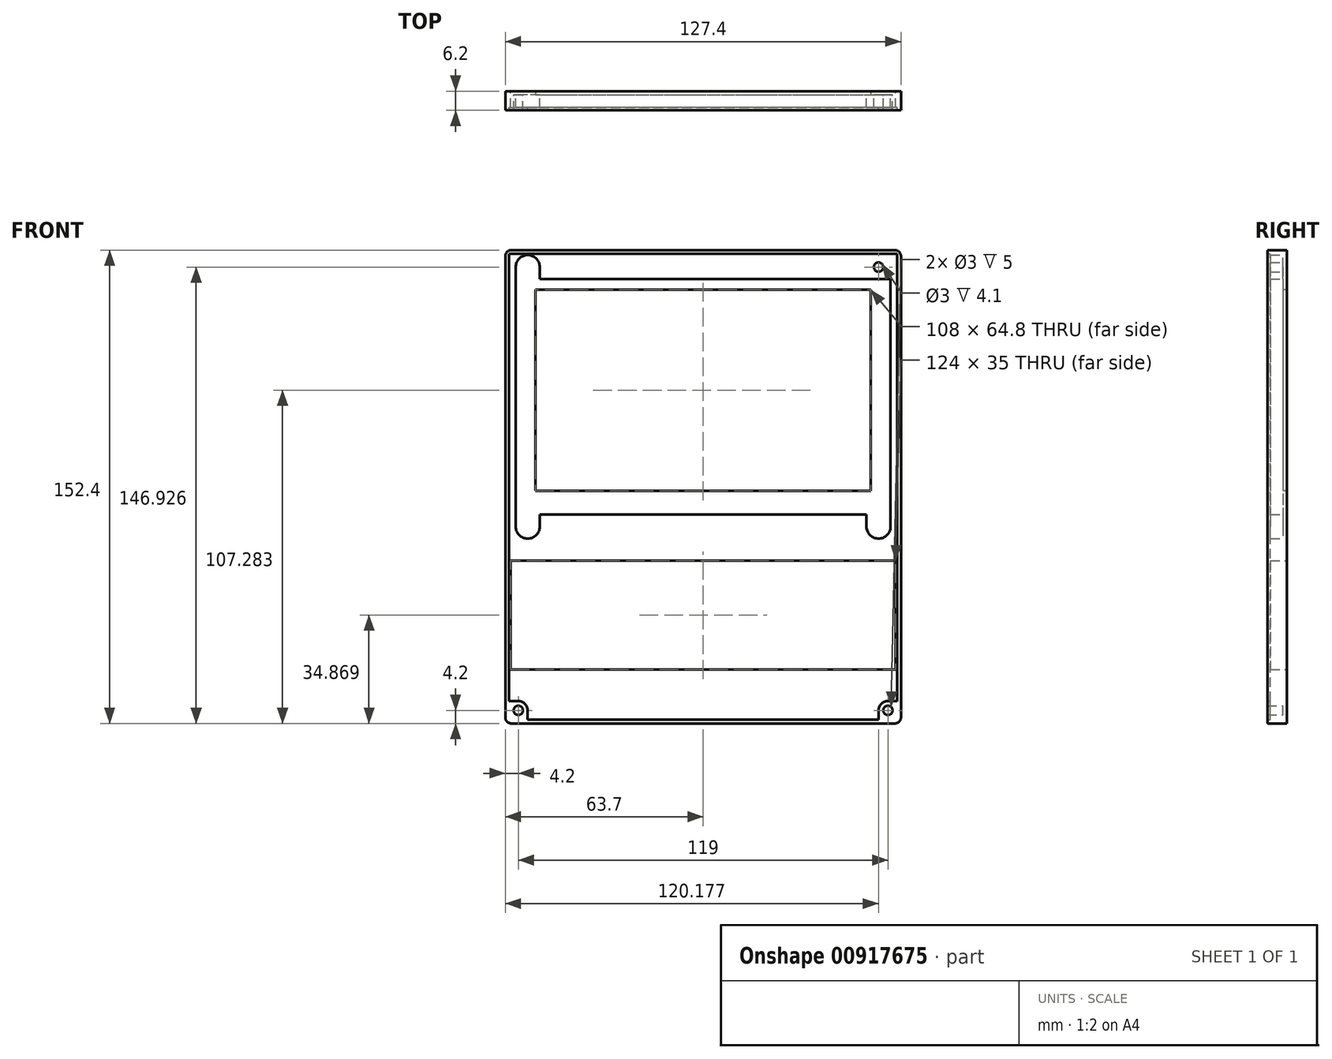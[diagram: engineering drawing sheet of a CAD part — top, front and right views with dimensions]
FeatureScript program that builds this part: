
annotation { "Feature Type Name" : "Feature", "Feature Type Description" : "" }
export const myFeature = defineFeature(function(context is Context, id is Id, definition is map)
    precondition{}
    {
        {
            var Q0;
            Q0=qCreatedBy(makeId("Front.planeOp"),FACE);
            var sketch = newSketch(context, id + "F0", { "sketchPlane" : qUnion([Q0])});
            skLineSegment(sketch, "E0.bottom", {"start": v(0, 0) * mm, "end": v(125, 0) * mm});
            skLineSegment(sketch, "E0.top", {"start": v(0, -150) * mm, "end": v(125, -150) * mm});
            skLineSegment(sketch, "E0.left", {"start": v(0, 0) * mm, "end": v(0, -150) * mm});
            skLineSegment(sketch, "E0.right", {"start": v(125, 0) * mm, "end": v(125, -150) * mm});
            skLineSegment(sketch, "E1.0", {"start": v(-1.2, 1.2) * mm, "end": v(126.2, 1.2) * mm});
            skLineSegment(sketch, "E1.1", {"start": v(-1.2, 1.2) * mm, "end": v(-1.2, -151.2) * mm});
            skLineSegment(sketch, "E1.2", {"start": v(-1.2, -151.2) * mm, "end": v(126.2, -151.2) * mm});
            skLineSegment(sketch, "E1.3", {"start": v(126.2, 1.2) * mm, "end": v(126.2, -151.2) * mm});
            skSolve(sketch);
        }
        {
            var Q0;
            Q0=makeQuery(id+"F0.imprint","IMPRINT",FACE,{"disambiguationData":[TD([[makeQuery(id+"F0.imprint","IMPRINT",EDGE,{"derivedFrom":sQuery(id+"F0.wireOp",EDGE,"E0.bottom")}),1.0]])]});
            var Q1;
            Q1=makeQuery(id+"F0.imprint","IMPRINT",FACE,{"disambiguationData":[TD([[makeQuery(id+"F0.imprint","IMPRINT",EDGE,{"derivedFrom":sQuery(id+"F0.wireOp",EDGE,"E0.bottom")}),-1.0]])]});
            extrude(context, id + "F1", {"entities" : qUnion([Q0, Q1]), "depth" : 1.2 * mm, "offsetDistance" : 25 * mm});
        }
        {
            var Q0;
            Q0=makeQuery(id+"F0.imprint","IMPRINT",FACE,{"disambiguationData":[TD([[makeQuery(id+"F0.imprint","IMPRINT",EDGE,{"derivedFrom":sQuery(id+"F0.wireOp",EDGE,"E0.bottom")}),1.0]])]});
            extrude(context, id + "F2", {"entities" : qUnion([Q0]), "operationType" : NewBodyOperationType.ADD, "depth" : 6.2 * mm, "offsetDistance" : 25 * mm});
        }
        {
            var Q0;
            Q0=makeQuery(id+"F1.opExtrude","CAP_FACE",FACE,{"disambiguationData":[OSD([sQuery(id+"F0.wireOp",EDGE,"E1.0"),sQuery(id+"F0.wireOp",EDGE,"E1.1"),sQuery(id+"F0.wireOp",EDGE,"E1.2"),sQuery(id+"F0.wireOp",EDGE,"E1.3")])],"isStart":false});
            var sketch = newSketch(context, id + "F3", { "sketchPlane" : qUnion([Q0])});
            skLineSegment(sketch, "E2", {"start": v(62.5, 0) * mm, "end": v(62.5, -150) * mm, "construction": true});
            skLineSegment(sketch, "E3", {"start": v(0, -75) * mm, "end": v(125, -75) * mm, "construction": true});
            skLineSegment(sketch, "E4.bottom", {"start": v(8.5, -11.52) * mm, "end": v(116.5, -11.52) * mm});
            skLineSegment(sketch, "E4.top", {"start": v(8.5, -76.32) * mm, "end": v(116.5, -76.32) * mm});
            skLineSegment(sketch, "E4.left", {"start": v(8.5, -11.52) * mm, "end": v(8.5, -76.32) * mm});
            skLineSegment(sketch, "E4.right", {"start": v(116.5, -11.52) * mm, "end": v(116.5, -76.32) * mm});
            skPoint(sketch, "E5", {"position": v(62.5, -11.52) * mm});
            skLineSegment(sketch, "E6.bottom", {"start": v(2.15, -8.15) * mm, "end": v(122.85, -8.15) * mm});
            skLineSegment(sketch, "E6.top", {"start": v(2.15, -83.95) * mm, "end": v(122.85, -83.95) * mm});
            skLineSegment(sketch, "E6.left", {"start": v(2.15, -8.15) * mm, "end": v(2.15, -83.95) * mm});
            skLineSegment(sketch, "E6.right", {"start": v(122.85, -8.15) * mm, "end": v(122.85, -83.95) * mm});
            skLineSegment(sketch, "E7.bottom", {"start": v(2.15, -8.15) * mm, "end": v(9.9, -8.15) * mm});
            skLineSegment(sketch, "E7.top", {"start": v(6.02, -0.4) * mm, "end": v(6.03, -0.4) * mm});
            skLineSegment(sketch, "E7.left", {"start": v(2.15, -8.15) * mm, "end": v(2.15, -4.27) * mm});
            skLineSegment(sketch, "E7.right", {"start": v(9.9, -8.15) * mm, "end": v(9.9, -4.27) * mm});
            skLineSegment(sketch, "E8.MirrorCS", {"start": v(115.1, -8.15) * mm, "end": v(115.1, -4.27) * mm});
            skLineSegment(sketch, "E9.MirrorCS", {"start": v(122.85, -8.15) * mm, "end": v(115.1, -8.15) * mm});
            skLineSegment(sketch, "E10.MirrorCS", {"start": v(122.85, -8.15) * mm, "end": v(122.85, -4.27) * mm});
            skLineSegment(sketch, "E11.MirrorCS", {"start": v(118.98, -0.4) * mm, "end": v(118.97, -0.4) * mm});
            skLineSegment(sketch, "E12.bottom", {"start": v(0.5, -98.83) * mm, "end": v(124.5, -98.83) * mm});
            skLineSegment(sketch, "E12.top", {"start": v(0.5, -133.83) * mm, "end": v(124.5, -133.83) * mm});
            skLineSegment(sketch, "E12.left", {"start": v(0.5, -98.83) * mm, "end": v(0.5, -133.83) * mm});
            skLineSegment(sketch, "E12.right", {"start": v(124.5, -98.83) * mm, "end": v(124.5, -133.83) * mm});
            skPoint(sketch, "E13", {"position": v(62.5, -98.83) * mm});
            skLineSegment(sketch, "E14", {"start": v(6.02, -0.4) * mm, "end": v(6.02, -8.15) * mm, "construction": true});
            skLineSegment(sketch, "E15", {"start": v(2.15, -4.27) * mm, "end": v(9.9, -4.27) * mm, "construction": true});
            skCircle(sketch, "E16", {"center": v(6.02, -4.27) * mm, "radius": 1.5 * mm});
            skLineSegment(sketch, "E17", {"start": v(118.98, -0.4) * mm, "end": v(118.98, -8.15) * mm, "construction": true});
            skLineSegment(sketch, "E18", {"start": v(115.1, -4.27) * mm, "end": v(122.85, -4.27) * mm, "construction": true});
            skCircle(sketch, "E19", {"center": v(118.98, -4.27) * mm, "radius": 1.5 * mm});
            skPoint(sketch, "E20.visualSharp", {"position": v(9.9, -0.4) * mm});
            skArc(sketch, "E20.filletArc", {"start": v(9.9, -4.27) * mm, "mid": v(8.76, -1.53) * mm, "end": v(6.03, -0.4) * mm});
            skPoint(sketch, "E21.visualSharp", {"position": v(2.15, -0.4) * mm});
            skArc(sketch, "E21.filletArc", {"start": v(6.02, -0.4) * mm, "mid": v(3.28, -1.53) * mm, "end": v(2.15, -4.27) * mm});
            skPoint(sketch, "E22.visualSharp", {"position": v(115.1, -0.4) * mm});
            skArc(sketch, "E22.filletArc", {"start": v(118.97, -0.4) * mm, "mid": v(116.24, -1.53) * mm, "end": v(115.1, -4.27) * mm});
            skPoint(sketch, "E23.visualSharp", {"position": v(122.85, -0.4) * mm});
            skArc(sketch, "E23.filletArc", {"start": v(122.85, -4.27) * mm, "mid": v(121.72, -1.53) * mm, "end": v(118.98, -0.4) * mm});
            skLineSegment(sketch, "E24", {"start": v(122.85, -46.05) * mm, "end": v(2.15, -46.05) * mm, "construction": true});
            skArc(sketch, "E25.MirrorCS", {"start": v(6.02, -91.7) * mm, "mid": v(3.28, -90.56) * mm, "end": v(2.15, -87.82) * mm});
            skLineSegment(sketch, "E26.MirrorCS", {"start": v(6.02, -91.7) * mm, "end": v(6.03, -91.7) * mm});
            skArc(sketch, "E27.MirrorCS", {"start": v(9.9, -87.82) * mm, "mid": v(8.76, -90.56) * mm, "end": v(6.03, -91.7) * mm});
            skLineSegment(sketch, "E28.MirrorCS", {"start": v(9.9, -83.95) * mm, "end": v(9.9, -87.82) * mm});
            skLineSegment(sketch, "E29.MirrorCS", {"start": v(2.15, -83.95) * mm, "end": v(2.15, -87.82) * mm});
            skCircle(sketch, "E30.MirrorC", {"center": v(6.02, -87.82) * mm, "radius": 1.5 * mm});
            skArc(sketch, "E31.MirrorCS", {"start": v(118.97, -91.7) * mm, "mid": v(116.24, -90.56) * mm, "end": v(115.1, -87.82) * mm});
            skLineSegment(sketch, "E32.MirrorCS", {"start": v(118.98, -91.7) * mm, "end": v(118.97, -91.7) * mm});
            skArc(sketch, "E33.MirrorCS", {"start": v(122.85, -87.82) * mm, "mid": v(121.72, -90.56) * mm, "end": v(118.98, -91.7) * mm});
            skLineSegment(sketch, "E34.MirrorCS", {"start": v(122.85, -83.95) * mm, "end": v(122.85, -87.82) * mm});
            skLineSegment(sketch, "E35.MirrorCS", {"start": v(115.1, -83.95) * mm, "end": v(115.1, -87.82) * mm});
            skCircle(sketch, "E36.MirrorC", {"center": v(118.98, -87.82) * mm, "radius": 1.5 * mm});
            skLineSegment(sketch, "E37.bottom", {"start": v(0, -150) * mm, "end": v(6, -150) * mm});
            skLineSegment(sketch, "E37.top", {"start": v(0, -144) * mm, "end": v(3, -144) * mm});
            skLineSegment(sketch, "E37.left", {"start": v(0, -150) * mm, "end": v(0, -144) * mm});
            skLineSegment(sketch, "E37.right", {"start": v(6, -150) * mm, "end": v(6, -147) * mm});
            skLineSegment(sketch, "E38", {"start": v(3, -144) * mm, "end": v(3, -150) * mm, "construction": true});
            skCircle(sketch, "E39", {"center": v(3, -147) * mm, "radius": 1.5 * mm});
            skPoint(sketch, "E40.visualSharp", {"position": v(6, -144) * mm});
            skArc(sketch, "E40.filletArc", {"start": v(6, -147) * mm, "mid": v(5.12, -144.88) * mm, "end": v(3, -144) * mm});
            skLineSegment(sketch, "E41.MirrorCS", {"start": v(125, -144) * mm, "end": v(122, -144) * mm});
            skArc(sketch, "E42.MirrorCS", {"start": v(119, -147) * mm, "mid": v(119.88, -144.88) * mm, "end": v(122, -144) * mm});
            skLineSegment(sketch, "E43.MirrorCS", {"start": v(119, -150) * mm, "end": v(119, -147) * mm});
            skLineSegment(sketch, "E44.MirrorCS", {"start": v(125, -150) * mm, "end": v(125, -144) * mm});
            skLineSegment(sketch, "E45.MirrorCS", {"start": v(125, -150) * mm, "end": v(119, -150) * mm});
            skCircle(sketch, "E46.MirrorC", {"center": v(122, -147) * mm, "radius": 1.5 * mm});
            skLineSegment(sketch, "E47.MirrorCS", {"start": v(122, -144) * mm, "end": v(122, -150) * mm, "construction": true});
            skSolve(sketch);
        }
        {
            var Q0;
            Q0=makeQuery(id+"F3.imprint","IMPRINT",FACE,{"disambiguationData":[TD([[makeQuery(id+"F3.imprint","IMPRINT",EDGE,{"derivedFrom":sQuery(id+"F3.wireOp",EDGE,"E4.bottom")}),-1.0]])]});
            extrude(context, id + "F4", {"entities" : qUnion([Q0]), "operationType" : NewBodyOperationType.REMOVE, "depth" : -1.2 * mm, "offsetDistance" : 25 * mm});
        }
        {
            var Q0;
            Q0=makeQuery(id+"F3.imprint","IMPRINT",FACE,{"disambiguationData":[TD([[makeQuery(id+"F3.imprint","IMPRINT",EDGE,{"derivedFrom":sQuery(id+"F3.wireOp",EDGE,"E7.bottom")}),1.0]])]});
            var Q1;
            Q1=makeQuery(id+"F3.imprint","IMPRINT",FACE,{"disambiguationData":[TD([[makeQuery(id+"F3.imprint","IMPRINT",EDGE,{"derivedFrom":sQuery(id+"F3.wireOp",EDGE,"E8.MirrorCS")}),-1.0]])]});
            var Q2;
            Q2=makeQuery(id+"F3.imprint","IMPRINT",FACE,{"disambiguationData":[TD([[makeQuery(id+"F3.imprint","IMPRINT",EDGE,{"derivedFrom":sQuery(id+"F3.wireOp",EDGE,"E31.MirrorCS")}),-1.0]])]});
            var Q3;
            Q3=makeQuery(id+"F3.imprint","IMPRINT",FACE,{"disambiguationData":[TD([[makeQuery(id+"F3.imprint","IMPRINT",EDGE,{"derivedFrom":sQuery(id+"F3.wireOp",EDGE,"E25.MirrorCS")}),-1.0]])]});
            extrude(context, id + "F5", {"entities" : qUnion([Q0, Q1, Q2, Q3]), "operationType" : NewBodyOperationType.ADD, "depth" : 4.1 * mm, "offsetDistance" : 25 * mm});
        }
        {
            var Q0;
            {var subQ0=sQuery(id+"F0.wireOp",EDGE,"E1.3");var subQ1=sQuery(id+"F0.wireOp",EDGE,"E1.2");Q0=makeQuery(id+"F2.boolean.opBoolean","MERGE",EDGE,{"derivedFrom":[makeQuery(id+"F1.opExtrude","SWEPT_EDGE",EDGE,{"disambiguationData":[OSD([subQ1,subQ0])]}),makeQuery(id+"F2.opExtrude","SWEPT_EDGE",EDGE,{"disambiguationData":[OSD([subQ1,subQ0])]})]});}
            var Q1;
            {var subQ0=sQuery(id+"F0.wireOp",EDGE,"E1.3");var subQ1=sQuery(id+"F0.wireOp",EDGE,"E1.0");Q1=makeQuery(id+"F2.boolean.opBoolean","MERGE",EDGE,{"derivedFrom":[makeQuery(id+"F1.opExtrude","SWEPT_EDGE",EDGE,{"disambiguationData":[OSD([subQ1,subQ0])]}),makeQuery(id+"F2.opExtrude","SWEPT_EDGE",EDGE,{"disambiguationData":[OSD([subQ1,subQ0])]})]});}
            var Q2;
            {var subQ0=sQuery(id+"F0.wireOp",EDGE,"E1.1");var subQ1=sQuery(id+"F0.wireOp",EDGE,"E1.0");Q2=makeQuery(id+"F2.boolean.opBoolean","MERGE",EDGE,{"derivedFrom":[makeQuery(id+"F1.opExtrude","SWEPT_EDGE",EDGE,{"disambiguationData":[OSD([subQ1,subQ0])]}),makeQuery(id+"F2.opExtrude","SWEPT_EDGE",EDGE,{"disambiguationData":[OSD([subQ1,subQ0])]})]});}
            var Q3;
            {var subQ0=sQuery(id+"F0.wireOp",EDGE,"E1.2");var subQ1=sQuery(id+"F0.wireOp",EDGE,"E1.1");Q3=makeQuery(id+"F2.boolean.opBoolean","MERGE",EDGE,{"derivedFrom":[makeQuery(id+"F1.opExtrude","SWEPT_EDGE",EDGE,{"disambiguationData":[OSD([subQ1,subQ0])]}),makeQuery(id+"F2.opExtrude","SWEPT_EDGE",EDGE,{"disambiguationData":[OSD([subQ1,subQ0])]})]});}
            fillet(context, id + "F6", {"entities" : qUnion([Q0, Q1, Q2, Q3]), "radius" : 2 * mm, "tangentPropagation" : true, "allowEdgeOverflow" : false});
        }
        {
            var Q0;
            Q0=makeQuery(id+"F3.imprint","IMPRINT",FACE,{"disambiguationData":[TD([[makeQuery(id+"F3.imprint","IMPRINT",EDGE,{"derivedFrom":sQuery(id+"F3.wireOp",EDGE,"E12.bottom")}),-1.0]])]});
            extrude(context, id + "F7", {"entities" : qUnion([Q0]), "operationType" : NewBodyOperationType.REMOVE, "oppositeDirection" : true, "depth" : 1.2 * mm, "offsetDistance" : 25 * mm});
        }
        {
            var Q0;
            Q0=makeQuery(id+"F3.imprint","IMPRINT",FACE,{"disambiguationData":[TD([[makeQuery(id+"F3.imprint","IMPRINT",EDGE,{"derivedFrom":sQuery(id+"F3.wireOp",EDGE,"E41.MirrorCS")}),1.0]])]});
            var Q1;
            Q1=makeQuery(id+"F3.imprint","IMPRINT",FACE,{"disambiguationData":[TD([[makeQuery(id+"F3.imprint","IMPRINT",EDGE,{"derivedFrom":sQuery(id+"F3.wireOp",EDGE,"E37.bottom")}),-1.0]])]});
            extrude(context, id + "F8", {"entities" : qUnion([Q0, Q1]), "operationType" : NewBodyOperationType.ADD, "depth" : 5 * mm, "offsetDistance" : 25 * mm});
        }
    });
